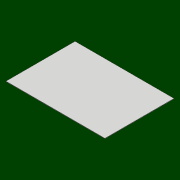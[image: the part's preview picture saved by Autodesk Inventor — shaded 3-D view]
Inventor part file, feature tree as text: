
AUTODESK INVENTOR PART (.ipt)
format: ipt  version: 2018 (Build 220112000, 112)  size: 72,192 bytes
history: native  units: mm
features: other x1, extrude x1, sketch x1
ambient origin geometry x8: Origin, YZ Plane, XZ Plane, XY Plane, X Axis, Y Axis, Z Axis, Center Point
bodies: Body1 (feature_tree)
feature tree (3):
  other  "ソリッド1"
  extrude  "押し出し1"  Depth=370.0mm
  sketch  "スケッチ1"
